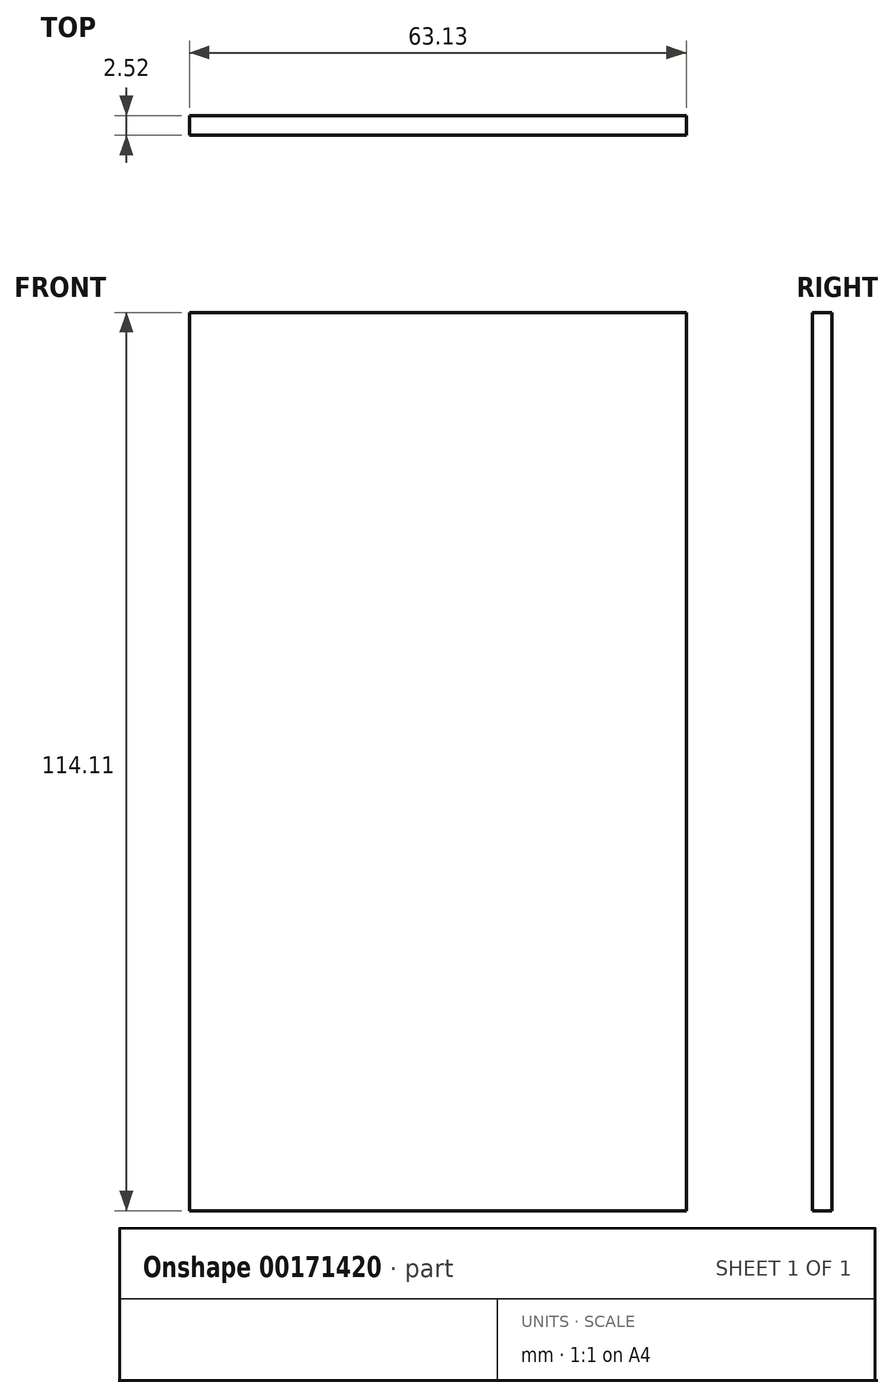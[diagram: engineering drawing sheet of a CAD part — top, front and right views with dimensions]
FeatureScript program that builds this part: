
annotation { "Feature Type Name" : "Feature", "Feature Type Description" : "" }
export const myFeature = defineFeature(function(context is Context, id is Id, definition is map)
    precondition{}
    {
        {
            var Q0;
            Q0=qCreatedBy(makeId("Front.planeOp"),FACE);
            var sketch = newSketch(context, id + "F0", { "sketchPlane" : qUnion([Q0])});
            skLineSegment(sketch, "E0.bottom", {"start": v(31.04, -43.89) * mm, "end": v(-32.09, -43.89) * mm});
            skLineSegment(sketch, "E0.top", {"start": v(31.04, 70.22) * mm, "end": v(-32.09, 70.22) * mm});
            skLineSegment(sketch, "E0.left", {"start": v(31.04, -43.89) * mm, "end": v(31.04, 70.22) * mm});
            skLineSegment(sketch, "E0.right", {"start": v(-32.09, -43.89) * mm, "end": v(-32.09, 70.22) * mm});
            skPoint(sketch, "E0.middle", {"position": v(-0.52, 13.17) * mm});
            skSolve(sketch);
        }
        {
            var Q0;
            Q0=makeQuery(id+"F0.imprint","IMPRINT",FACE,{"disambiguationData":[TD([[makeQuery(id+"F0.imprint","IMPRINT",EDGE,{"derivedFrom":sQuery(id+"F0.wireOp",EDGE,"E0.bottom")}),-1.0]])]});
            extrude(context, id + "F1", {"entities" : qUnion([Q0]), "depth" : 2.52 * mm});
        }
    });
